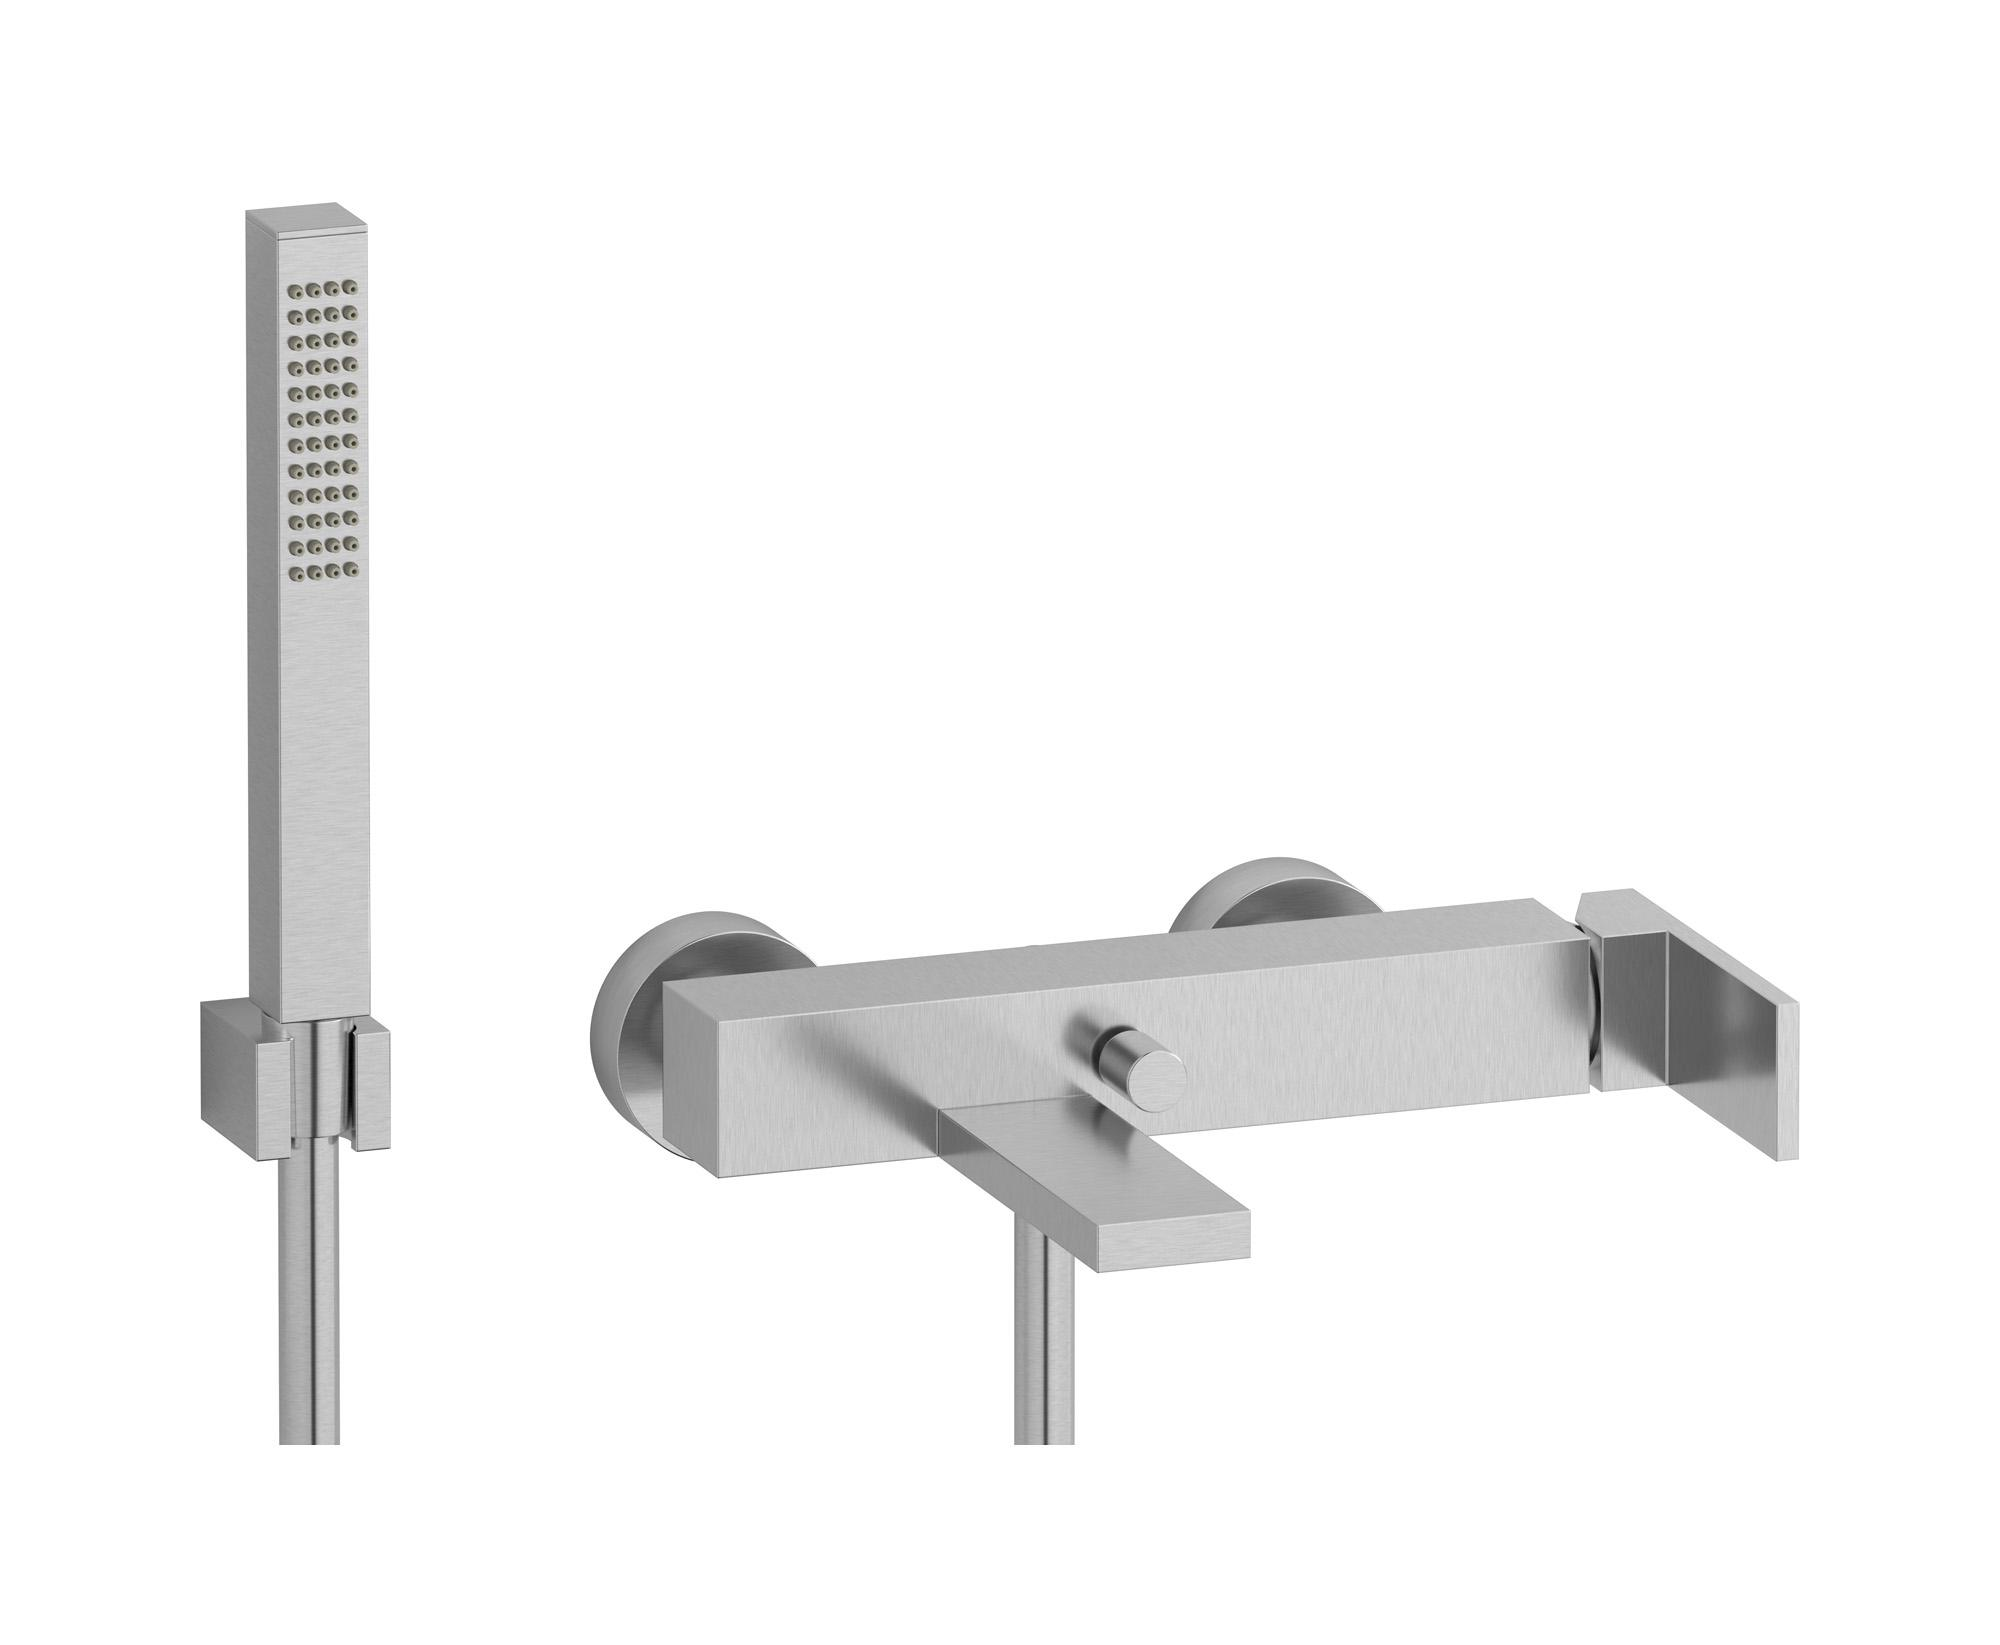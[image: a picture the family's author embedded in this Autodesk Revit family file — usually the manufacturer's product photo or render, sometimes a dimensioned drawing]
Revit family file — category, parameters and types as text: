
# Revit family: RU250
name_source: partatom
category: Apparecchi idraulici
units: mm (PartAtom-declared; Revit-internal decimal feet)

## family parameters
Basato su piano di lavoro = No
Condiviso = No
Mantieni orientamento annotazione = No
Numero OmniClass = 23.45.55.17
Punto di calcolo locali = No
Quota connettore circolare = Usa diametro
Sempre verticale = Sì
Taglio con vuoti quando caricato = No
Tipo di parte = Normale
Titolo OmniClass = Mixing Faucets

## types (12) — shared parameters
Cold water inlet = 10 mm  [stored 0.0328084 ft]
Commenti sul tipo = Wall mounted bath filler complete with shower kit
Connessione CW = No
Connessione HW = No
Connessione di scarico = No
Connessione di ventilazione = No
Descrizione = Wall mounted bath filler complete with shower kit
Hot water inlet = 10 mm  [stored 0.0328084 ft]
Produttore = IB Rubinetterie S.p.A.
URL = https://www.weareib.it
zero-valued in all types: Prospetto di default

## per-type parameters (varying)
| type | Finishes surface | Immagine tipo | Modello |
| Matt White | IB_matt white | RU250BO.jpg | RU250BO |
| Chrome | IB_Chrome | RU250CC.jpg | RU250CC |
| Black Chrome | IB_Black chrome | RU250CF.jpg | RU250CF |
| Brushed Black Chrome | IB_Brushed black chrome | RU250CS.jpg | RU250CS |
| Pale Gold | IB_Pale gold | RU250II.jpg | RU250II |
| Brushed Pale Gold | IB_brushed pale gold | RU250IS.jpg | RU250IS |
| Matt Black | IB_matt black | RU250NP.jpg | RU250NP |
| Gold | IB_gold | RU250OO.jpg | RU250OO |
| Brushed Gold | IB_brushed gold | RU250OS.jpg | RU250OS |
| Rose Gold | IB_Rose gold | RU250RS.jpg | RU250RS |
| Brushed Rose Gold | IB_Brushed rose gold | RU250SR.jpg | RU250SR |
| Brushed Nickel | IB_Brushed nickel | RU250SS.jpg | RU250SS |

note: [stored X ft] marks values corroborated as IEEE doubles in the binary element streams (Revit-internal decimal feet)
